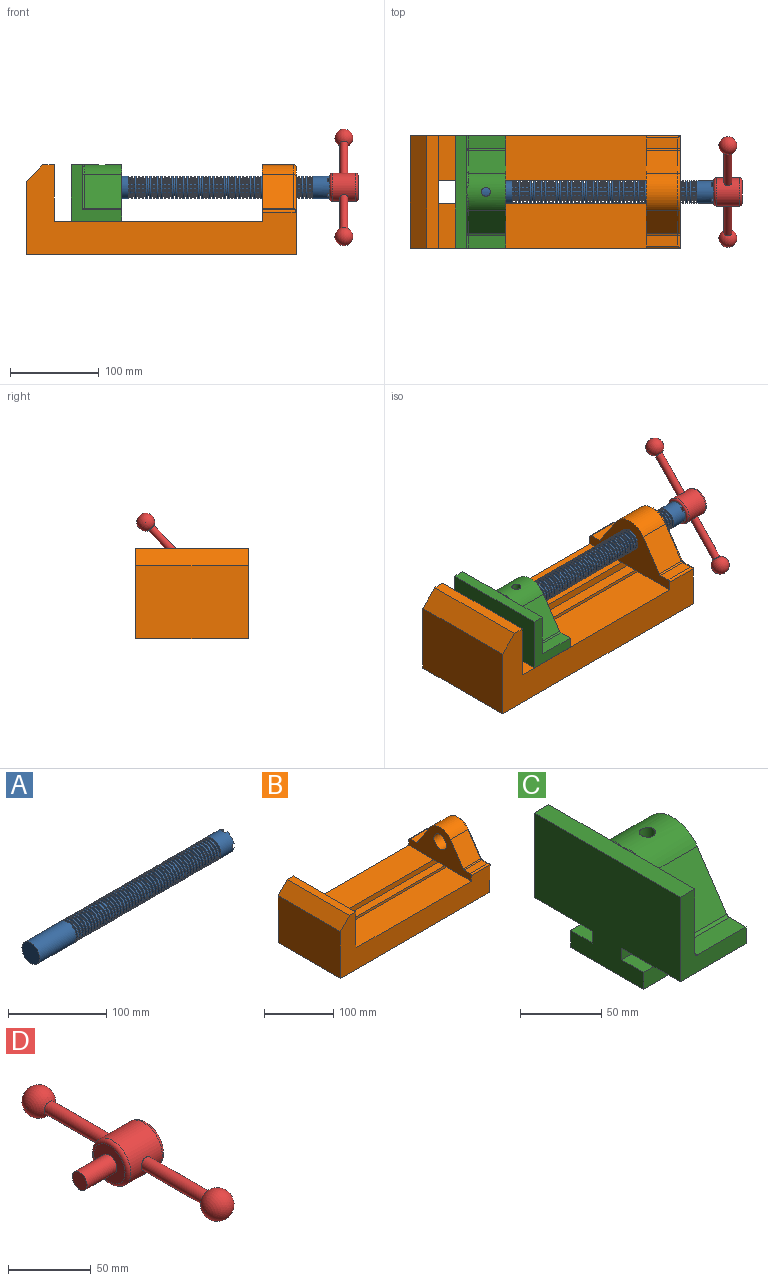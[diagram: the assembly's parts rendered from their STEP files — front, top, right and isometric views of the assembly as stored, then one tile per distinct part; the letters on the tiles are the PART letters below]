
ASSEMBLY  parts=4 mates=4
PART A: 220 faces, bbox 279.4x25.4x25.4 mm
  f0: cylinder r=12.7mm len=25.4mm, axis (-1,0,0), area 1468.2mm2, adj f1,f2,f3,f5,f7,f208,f209,f210
  f1: plane 9.9x9.9mm, normal (1,0,0), area 62.3mm2, adj f0,f4,f213,f216
  f2: plane 9.9x9.9mm, normal (1,0,0), area 62.3mm2, adj f0,f4,f210,f218
  f3: plane 9.9x9.9mm, normal (1,0,0), area 62.3mm2, adj f0,f4,f209,f212
  f4: cylinder r=6.35mm len=25.4mm, axis (1,0,0), area 960.3mm2, adj f1,f2,f3,f5,f6,f208,f209,f210
  f5: plane 9.9x9.9mm, normal (1,0,0), area 62.3mm2, adj f0,f4,f215,f217
  f6: plane 12.7x12.7mm, normal (1,0,0), area 126.7mm2, adj f4
  f7: cone r=12.7mm half-angle=76deg, axis (1,0,0), area 188mm2, adj f0,f9
  f8: cone r=10.16mm half-angle=76deg, axis (-1,0,0), area 188mm2, adj f9,f10
  f9: cylinder r=10.16mm len=20.32mm, axis (1,0,0), area 81.1mm2, adj f7,f8
  f10: cylinder r=12.7mm len=25.4mm, axis (-1,0,0), area 131.7mm2, adj f8,f11
  f11: cone r=12.7mm half-angle=76deg, axis (1,0,0), area 188mm2, adj f10,f13
  f12: cone r=10.16mm half-angle=76deg, axis (-1,0,0), area 188mm2, adj f13,f14
  f13: cylinder r=10.16mm len=20.32mm, axis (1,0,0), area 81.1mm2, adj f11,f12
  f14: cylinder r=12.7mm len=25.4mm, axis (-1,0,0), area 131.7mm2, adj f12,f15
  f15: cone r=12.7mm half-angle=76deg, axis (1,0,0), area 188mm2, adj f14,f17
  f16: cone r=10.16mm half-angle=76deg, axis (-1,0,0), area 188mm2, adj f17,f18
  f17: cylinder r=10.16mm len=20.32mm, axis (1,0,0), area 81.1mm2, adj f15,f16
  f18: cylinder r=12.7mm len=25.4mm, axis (-1,0,0), area 131.7mm2, adj f16,f19
  f19: cone r=12.7mm half-angle=76deg, axis (1,0,0), area 188mm2, adj f18,f21
  f20: cone r=10.16mm half-angle=76deg, axis (-1,0,0), area 188mm2, adj f21,f22
  f21: cylinder r=10.16mm len=20.32mm, axis (1,0,0), area 81.1mm2, adj f19,f20
  f22: cylinder r=12.7mm len=25.4mm, axis (-1,0,0), area 131.7mm2, adj f20,f23
  f23: cone r=12.7mm half-angle=76deg, axis (1,0,0), area 188mm2, adj f22,f25
  f24: cone r=10.16mm half-angle=76deg, axis (-1,0,0), area 188mm2, adj f25,f26
  f25: cylinder r=10.16mm len=20.32mm, axis (1,0,0), area 81.1mm2, adj f23,f24
  f26: cylinder r=12.7mm len=25.4mm, axis (-1,0,0), area 131.7mm2, adj f24,f27
  f27: cone r=12.7mm half-angle=76deg, axis (1,0,0), area 188mm2, adj f26,f29
  f28: cone r=10.16mm half-angle=76deg, axis (-1,0,0), area 188mm2, adj f29,f30
  f29: cylinder r=10.16mm len=20.32mm, axis (1,0,0), area 81.1mm2, adj f27,f28
  f30: cylinder r=12.7mm len=25.4mm, axis (-1,0,0), area 131.7mm2, adj f28,f31
  f31: cone r=12.7mm half-angle=76deg, axis (1,0,0), area 188mm2, adj f30,f33
  f32: cone r=10.16mm half-angle=76deg, axis (-1,0,0), area 188mm2, adj f33,f34
  f33: cylinder r=10.16mm len=20.32mm, axis (1,0,0), area 81.1mm2, adj f31,f32
  f34: cylinder r=12.7mm len=25.4mm, axis (-1,0,0), area 131.7mm2, adj f32,f35
  f35: cone r=12.7mm half-angle=76deg, axis (1,0,0), area 188mm2, adj f34,f37
  f36: cone r=10.16mm half-angle=76deg, axis (-1,0,0), area 188mm2, adj f37,f38
  f37: cylinder r=10.16mm len=20.32mm, axis (1,0,0), area 81.1mm2, adj f35,f36
  f38: cylinder r=12.7mm len=25.4mm, axis (-1,0,0), area 131.7mm2, adj f36,f39
  f39: cone r=12.7mm half-angle=76deg, axis (1,0,0), area 188mm2, adj f38,f41
  f40: cone r=10.16mm half-angle=76deg, axis (-1,0,0), area 188mm2, adj f41,f42
  f41: cylinder r=10.16mm len=20.32mm, axis (1,0,0), area 81.1mm2, adj f39,f40
  f42: cylinder r=12.7mm len=25.4mm, axis (-1,0,0), area 131.7mm2, adj f40,f43
  f43: cone r=12.7mm half-angle=76deg, axis (1,0,0), area 188mm2, adj f42,f45
  f44: cone r=10.16mm half-angle=76deg, axis (-1,0,0), area 188mm2, adj f45,f46
  f45: cylinder r=10.16mm len=20.32mm, axis (1,0,0), area 81.1mm2, adj f43,f44
  f46: cylinder r=12.7mm len=25.4mm, axis (-1,0,0), area 131.7mm2, adj f44,f47
  f47: cone r=12.7mm half-angle=76deg, axis (1,0,0), area 188mm2, adj f46,f49
  f48: cone r=10.16mm half-angle=76deg, axis (-1,0,0), area 188mm2, adj f49,f50
  f49: cylinder r=10.16mm len=20.32mm, axis (1,0,0), area 81.1mm2, adj f47,f48
  f50: cylinder r=12.7mm len=25.4mm, axis (-1,0,0), area 131.7mm2, adj f48,f51
  f51: cone r=12.7mm half-angle=76deg, axis (1,0,0), area 188mm2, adj f50,f53
  f52: cone r=10.16mm half-angle=76deg, axis (-1,0,0), area 188mm2, adj f53,f54
  f53: cylinder r=10.16mm len=20.32mm, axis (1,0,0), area 81.1mm2, adj f51,f52
  f54: cylinder r=12.7mm len=25.4mm, axis (-1,0,0), area 131.7mm2, adj f52,f55
  f55: cone r=12.7mm half-angle=76deg, axis (1,0,0), area 188mm2, adj f54,f57
  f56: cone r=10.16mm half-angle=76deg, axis (-1,0,0), area 188mm2, adj f57,f58
  f57: cylinder r=10.16mm len=20.32mm, axis (1,0,0), area 81.1mm2, adj f55,f56
  f58: cylinder r=12.7mm len=25.4mm, axis (-1,0,0), area 131.7mm2, adj f56,f59
  f59: cone r=12.7mm half-angle=76deg, axis (1,0,0), area 188mm2, adj f58,f61
  f60: cone r=10.16mm half-angle=76deg, axis (-1,0,0), area 188mm2, adj f61,f62
  f61: cylinder r=10.16mm len=20.32mm, axis (1,0,0), area 81.1mm2, adj f59,f60
  f62: cylinder r=12.7mm len=25.4mm, axis (-1,0,0), area 131.7mm2, adj f60,f63
  f63: cone r=12.7mm half-angle=76deg, axis (1,0,0), area 188mm2, adj f62,f65
  f64: cone r=10.16mm half-angle=76deg, axis (-1,0,0), area 188mm2, adj f65,f66
  f65: cylinder r=10.16mm len=20.32mm, axis (1,0,0), area 81.1mm2, adj f63,f64
  f66: cylinder r=12.7mm len=25.4mm, axis (-1,0,0), area 131.7mm2, adj f64,f67
  f67: cone r=12.7mm half-angle=76deg, axis (1,0,0), area 188mm2, adj f66,f69
  f68: cone r=10.16mm half-angle=76deg, axis (-1,0,0), area 188mm2, adj f69,f70
  f69: cylinder r=10.16mm len=20.32mm, axis (1,0,0), area 81.1mm2, adj f67,f68
  f70: cylinder r=12.7mm len=25.4mm, axis (-1,0,0), area 131.7mm2, adj f68,f71
  f71: cone r=12.7mm half-angle=76deg, axis (1,0,0), area 188mm2, adj f70,f73
  f72: cone r=10.16mm half-angle=76deg, axis (-1,0,0), area 188mm2, adj f73,f74
  f73: cylinder r=10.16mm len=20.32mm, axis (1,0,0), area 81.1mm2, adj f71,f72
  f74: cylinder r=12.7mm len=25.4mm, axis (-1,0,0), area 131.7mm2, adj f72,f75
  f75: cone r=12.7mm half-angle=76deg, axis (1,0,0), area 188mm2, adj f74,f77
  f76: cone r=10.16mm half-angle=76deg, axis (-1,0,0), area 188mm2, adj f77,f78
  f77: cylinder r=10.16mm len=20.32mm, axis (1,0,0), area 81.1mm2, adj f75,f76
  f78: cylinder r=12.7mm len=25.4mm, axis (-1,0,0), area 131.7mm2, adj f76,f79
  f79: cone r=12.7mm half-angle=76deg, axis (1,0,0), area 188mm2, adj f78,f81
  f80: cone r=10.16mm half-angle=76deg, axis (-1,0,0), area 188mm2, adj f81,f82
  f81: cylinder r=10.16mm len=20.32mm, axis (1,0,0), area 81.1mm2, adj f79,f80
  f82: cylinder r=12.7mm len=25.4mm, axis (-1,0,0), area 131.7mm2, adj f80,f83
  f83: cone r=12.7mm half-angle=76deg, axis (1,0,0), area 188mm2, adj f82,f85
  f84: cone r=10.16mm half-angle=76deg, axis (-1,0,0), area 188mm2, adj f85,f86
  f85: cylinder r=10.16mm len=20.32mm, axis (1,0,0), area 81.1mm2, adj f83,f84
  f86: cylinder r=12.7mm len=25.4mm, axis (-1,0,0), area 131.7mm2, adj f84,f87
  f87: cone r=12.7mm half-angle=76deg, axis (1,0,0), area 188mm2, adj f86,f89
  f88: cone r=10.16mm half-angle=76deg, axis (-1,0,0), area 188mm2, adj f89,f90
  f89: cylinder r=10.16mm len=20.32mm, axis (1,0,0), area 81.1mm2, adj f87,f88
  f90: cylinder r=12.7mm len=25.4mm, axis (-1,0,0), area 131.7mm2, adj f88,f91
  f91: cone r=12.7mm half-angle=76deg, axis (1,0,0), area 188mm2, adj f90,f93
  f92: cone r=10.16mm half-angle=76deg, axis (-1,0,0), area 188mm2, adj f93,f94
  f93: cylinder r=10.16mm len=20.32mm, axis (1,0,0), area 81.1mm2, adj f91,f92
  f94: cylinder r=12.7mm len=25.4mm, axis (-1,0,0), area 131.7mm2, adj f92,f95
  f95: cone r=12.7mm half-angle=76deg, axis (1,0,0), area 188mm2, adj f94,f97
  f96: cone r=10.16mm half-angle=76deg, axis (-1,0,0), area 188mm2, adj f97,f98
  f97: cylinder r=10.16mm len=20.32mm, axis (1,0,0), area 81.1mm2, adj f95,f96
  f98: cylinder r=12.7mm len=25.4mm, axis (-1,0,0), area 131.7mm2, adj f96,f99
  f99: cone r=12.7mm half-angle=76deg, axis (1,0,0), area 188mm2, adj f98,f101
  f100: cone r=10.16mm half-angle=76deg, axis (-1,0,0), area 188mm2, adj f101,f102
  f101: cylinder r=10.16mm len=20.32mm, axis (1,0,0), area 81.1mm2, adj f99,f100
  f102: cylinder r=12.7mm len=25.4mm, axis (-1,0,0), area 131.7mm2, adj f100,f103
  f103: cone r=12.7mm half-angle=76deg, axis (1,0,0), area 188mm2, adj f102,f105
  f104: cone r=10.16mm half-angle=76deg, axis (-1,0,0), area 188mm2, adj f105,f106
  f105: cylinder r=10.16mm len=20.32mm, axis (1,0,0), area 81.1mm2, adj f103,f104
  f106: cylinder r=12.7mm len=25.4mm, axis (-1,0,0), area 131.7mm2, adj f104,f107
  f107: cone r=12.7mm half-angle=76deg, axis (1,0,0), area 188mm2, adj f106,f109
  f108: cone r=10.16mm half-angle=76deg, axis (-1,0,0), area 188mm2, adj f109,f110
  f109: cylinder r=10.16mm len=20.32mm, axis (1,0,0), area 81.1mm2, adj f107,f108
  f110: cylinder r=12.7mm len=25.4mm, axis (-1,0,0), area 131.7mm2, adj f108,f111
  f111: cone r=12.7mm half-angle=76deg, axis (1,0,0), area 188mm2, adj f110,f113
  f112: cone r=10.16mm half-angle=76deg, axis (-1,0,0), area 188mm2, adj f113,f114
  f113: cylinder r=10.16mm len=20.32mm, axis (1,0,0), area 81.1mm2, adj f111,f112
  f114: cylinder r=12.7mm len=25.4mm, axis (-1,0,0), area 131.7mm2, adj f112,f115
  f115: cone r=12.7mm half-angle=76deg, axis (1,0,0), area 188mm2, adj f114,f117
  f116: cone r=10.16mm half-angle=76deg, axis (-1,0,0), area 188mm2, adj f117,f118
  f117: cylinder r=10.16mm len=20.32mm, axis (1,0,0), area 81.1mm2, adj f115,f116
  f118: cylinder r=12.7mm len=25.4mm, axis (-1,0,0), area 131.7mm2, adj f116,f119
  f119: cone r=12.7mm half-angle=76deg, axis (1,0,0), area 188mm2, adj f118,f121
  f120: cone r=10.16mm half-angle=76deg, axis (-1,0,0), area 188mm2, adj f121,f122
  f121: cylinder r=10.16mm len=20.32mm, axis (1,0,0), area 81.1mm2, adj f119,f120
  f122: cylinder r=12.7mm len=25.4mm, axis (-1,0,0), area 131.7mm2, adj f120,f123
  f123: cone r=12.7mm half-angle=76deg, axis (1,0,0), area 188mm2, adj f122,f125
  f124: cone r=10.16mm half-angle=76deg, axis (-1,0,0), area 188mm2, adj f125,f126
  f125: cylinder r=10.16mm len=20.32mm, axis (1,0,0), area 81.1mm2, adj f123,f124
  f126: cylinder r=12.7mm len=25.4mm, axis (-1,0,0), area 131.7mm2, adj f124,f127
  f127: cone r=12.7mm half-angle=76deg, axis (1,0,0), area 188mm2, adj f126,f129
  f128: cone r=10.16mm half-angle=76deg, axis (-1,0,0), area 188mm2, adj f129,f130
  f129: cylinder r=10.16mm len=20.32mm, axis (1,0,0), area 81.1mm2, adj f127,f128
  f130: cylinder r=12.7mm len=25.4mm, axis (-1,0,0), area 131.7mm2, adj f128,f131
  f131: cone r=12.7mm half-angle=76deg, axis (1,0,0), area 188mm2, adj f130,f133
  f132: cone r=10.16mm half-angle=76deg, axis (-1,0,0), area 188mm2, adj f133,f134
  f133: cylinder r=10.16mm len=20.32mm, axis (1,0,0), area 81.1mm2, adj f131,f132
  f134: cylinder r=12.7mm len=25.4mm, axis (-1,0,0), area 131.7mm2, adj f132,f135
  f135: cone r=12.7mm half-angle=76deg, axis (1,0,0), area 188mm2, adj f134,f137
  f136: cone r=10.16mm half-angle=76deg, axis (-1,0,0), area 188mm2, adj f137,f138
  f137: cylinder r=10.16mm len=20.32mm, axis (1,0,0), area 81.1mm2, adj f135,f136
  f138: cylinder r=12.7mm len=25.4mm, axis (-1,0,0), area 131.7mm2, adj f136,f139
  f139: cone r=12.7mm half-angle=76deg, axis (1,0,0), area 188mm2, adj f138,f141
  f140: cone r=10.16mm half-angle=76deg, axis (-1,0,0), area 188mm2, adj f141,f142
  f141: cylinder r=10.16mm len=20.32mm, axis (1,0,0), area 81.1mm2, adj f139,f140
  f142: cylinder r=12.7mm len=25.4mm, axis (-1,0,0), area 131.7mm2, adj f140,f143
  f143: cone r=12.7mm half-angle=76deg, axis (1,0,0), area 188mm2, adj f142,f145
  f144: cone r=10.16mm half-angle=76deg, axis (-1,0,0), area 188mm2, adj f145,f146
  f145: cylinder r=10.16mm len=20.32mm, axis (1,0,0), area 81.1mm2, adj f143,f144
  f146: cylinder r=12.7mm len=25.4mm, axis (-1,0,0), area 131.7mm2, adj f144,f147
  f147: cone r=12.7mm half-angle=76deg, axis (1,0,0), area 188mm2, adj f146,f149
  f148: cone r=10.16mm half-angle=76deg, axis (-1,0,0), area 188mm2, adj f149,f150
  f149: cylinder r=10.16mm len=20.32mm, axis (1,0,0), area 81.1mm2, adj f147,f148
  f150: cylinder r=12.7mm len=25.4mm, axis (-1,0,0), area 131.7mm2, adj f148,f151
  f151: cone r=12.7mm half-angle=76deg, axis (1,0,0), area 188mm2, adj f150,f153
  f152: cone r=10.16mm half-angle=76deg, axis (-1,0,0), area 188mm2, adj f153,f154
  f153: cylinder r=10.16mm len=20.32mm, axis (1,0,0), area 81.1mm2, adj f151,f152
  f154: cylinder r=12.7mm len=25.4mm, axis (-1,0,0), area 131.7mm2, adj f152,f155
  f155: cone r=12.7mm half-angle=76deg, axis (1,0,0), area 188mm2, adj f154,f157
  f156: cone r=10.16mm half-angle=76deg, axis (-1,0,0), area 188mm2, adj f157,f158
  f157: cylinder r=10.16mm len=20.32mm, axis (1,0,0), area 81.1mm2, adj f155,f156
  f158: cylinder r=12.7mm len=25.4mm, axis (-1,0,0), area 131.7mm2, adj f156,f159
  f159: cone r=12.7mm half-angle=76deg, axis (1,0,0), area 188mm2, adj f158,f161
  f160: cone r=10.16mm half-angle=76deg, axis (-1,0,0), area 188mm2, adj f161,f162
  f161: cylinder r=10.16mm len=20.32mm, axis (1,0,0), area 81.1mm2, adj f159,f160
  f162: cylinder r=12.7mm len=25.4mm, axis (-1,0,0), area 131.7mm2, adj f160,f163
  f163: cone r=12.7mm half-angle=76deg, axis (1,0,0), area 188mm2, adj f162,f165
  f164: cone r=10.16mm half-angle=76deg, axis (-1,0,0), area 188mm2, adj f165,f166
  f165: cylinder r=10.16mm len=20.32mm, axis (1,0,0), area 81.1mm2, adj f163,f164
  f166: cylinder r=12.7mm len=25.4mm, axis (-1,0,0), area 131.7mm2, adj f164,f167
  f167: cone r=12.7mm half-angle=76deg, axis (1,0,0), area 188mm2, adj f166,f169
  f168: cone r=10.16mm half-angle=76deg, axis (-1,0,0), area 188mm2, adj f169,f170
  f169: cylinder r=10.16mm len=20.32mm, axis (1,0,0), area 81.1mm2, adj f167,f168
  f170: cylinder r=12.7mm len=25.4mm, axis (-1,0,0), area 131.7mm2, adj f168,f171
  f171: cone r=12.7mm half-angle=76deg, axis (1,0,0), area 188mm2, adj f170,f173
  f172: cone r=10.16mm half-angle=76deg, axis (-1,0,0), area 188mm2, adj f173,f174
  f173: cylinder r=10.16mm len=20.32mm, axis (1,0,0), area 81.1mm2, adj f171,f172
  f174: cylinder r=12.7mm len=25.4mm, axis (-1,0,0), area 131.7mm2, adj f172,f175
  f175: cone r=12.7mm half-angle=76deg, axis (1,0,0), area 188mm2, adj f174,f177
  f176: cone r=10.16mm half-angle=76deg, axis (-1,0,0), area 188mm2, adj f177,f178
  f177: cylinder r=10.16mm len=20.32mm, axis (1,0,0), area 81.1mm2, adj f175,f176
  f178: cylinder r=12.7mm len=25.4mm, axis (-1,0,0), area 131.7mm2, adj f176,f179
  f179: cone r=12.7mm half-angle=76deg, axis (1,0,0), area 188mm2, adj f178,f181
  f180: cone r=10.16mm half-angle=76deg, axis (-1,0,0), area 188mm2, adj f181,f182
  f181: cylinder r=10.16mm len=20.32mm, axis (1,0,0), area 81.1mm2, adj f179,f180
  f182: cylinder r=12.7mm len=25.4mm, axis (-1,0,0), area 131.7mm2, adj f180,f183
  f183: cone r=12.7mm half-angle=76deg, axis (1,0,0), area 188mm2, adj f182,f185
  f184: cone r=10.16mm half-angle=76deg, axis (-1,0,0), area 188mm2, adj f185,f186
  f185: cylinder r=10.16mm len=20.32mm, axis (1,0,0), area 81.1mm2, adj f183,f184
  f186: cylinder r=12.7mm len=25.4mm, axis (-1,0,0), area 131.7mm2, adj f184,f187
  f187: cone r=12.7mm half-angle=76deg, axis (1,0,0), area 188mm2, adj f186,f189
  f188: cone r=10.16mm half-angle=76deg, axis (-1,0,0), area 188mm2, adj f189,f190
  f189: cylinder r=10.16mm len=20.32mm, axis (1,0,0), area 81.1mm2, adj f187,f188
  f190: cylinder r=12.7mm len=25.4mm, axis (-1,0,0), area 131.7mm2, adj f188,f191
  f191: cone r=12.7mm half-angle=76deg, axis (1,0,0), area 188mm2, adj f190,f193
  f192: cone r=10.16mm half-angle=76deg, axis (-1,0,0), area 188mm2, adj f193,f194
  f193: cylinder r=10.16mm len=20.32mm, axis (1,0,0), area 81.1mm2, adj f191,f192
  f194: cylinder r=12.7mm len=25.4mm, axis (-1,0,0), area 131.7mm2, adj f192,f195
  f195: cone r=12.7mm half-angle=76deg, axis (1,0,0), area 188mm2, adj f194,f197
  f196: cone r=10.16mm half-angle=76deg, axis (-1,0,0), area 188mm2, adj f197,f198
  f197: cylinder r=10.16mm len=20.32mm, axis (1,0,0), area 81.1mm2, adj f195,f196
  f198: cylinder r=12.7mm len=25.4mm, axis (-1,0,0), area 131.7mm2, adj f196,f199
  f199: cone r=12.7mm half-angle=76deg, axis (1,0,0), area 188mm2, adj f198,f201
  f200: cone r=10.16mm half-angle=76deg, axis (-1,0,0), area 188mm2, adj f201,f202
  f201: cylinder r=10.16mm len=20.32mm, axis (1,0,0), area 81.1mm2, adj f199,f200
  f202: cylinder r=12.7mm len=25.4mm, axis (-1,0,0), area 131.7mm2, adj f200,f203
  f203: cone r=12.7mm half-angle=76deg, axis (1,0,0), area 188mm2, adj f202,f205
  f204: cone r=10.16mm half-angle=76deg, axis (-1,0,0), area 188mm2, adj f205,f207
  f205: cylinder r=10.16mm len=20.32mm, axis (1,0,0), area 81.1mm2, adj f203,f204
  f206: plane 25.4x25.4mm, normal (-1,0,0), area 506.7mm2, adj f207
  f207: cylinder r=12.7mm len=52.45mm, axis (-1,0,0), area 4185.4mm2, adj f204,f206
  f208: plane 6.88x5.08mm, normal (1,0,0), area 32.7mm2, adj f0,f4,f209,f210
  f209: plane 6.62x2.54mm, normal (0,-1,0), area 16.8mm2, adj f0,f3,f4,f208
  f210: plane 6.62x2.54mm, normal (0,1,0), area 16.8mm2, adj f0,f2,f4,f208
  f211: plane 6.88x5.08mm, normal (1,0,0), area 32.7mm2, adj f0,f4,f212,f213
  f212: plane 6.62x2.54mm, normal (0,0,1), area 16.8mm2, adj f0,f3,f4,f211
  f213: plane 6.62x2.54mm, normal (0,0,-1), area 16.8mm2, adj f0,f1,f4,f211
  f214: plane 6.88x5.08mm, normal (1,0,0), area 32.7mm2, adj f0,f4,f215,f216
  f215: plane 6.62x2.54mm, normal (0,1,0), area 16.8mm2, adj f0,f4,f5,f214
  f216: plane 6.62x2.54mm, normal (0,-1,0), area 16.8mm2, adj f0,f1,f4,f214
  f217: plane 6.62x2.54mm, normal (0,0,-1), area 16.8mm2, adj f0,f4,f5,f219
  f218: plane 6.62x2.54mm, normal (0,0,1), area 16.8mm2, adj f0,f2,f4,f219
  f219: plane 6.88x5.08mm, normal (1,0,0), area 32.7mm2, adj f0,f4,f217,f218
PART B: 39 faces, bbox 304.8x127x103.7 mm
  f0: plane 234.95x50.8mm, normal (0,0,1), area 11935.5mm2, adj f2,f8,f16,f26
  f1: plane 234.95x50.8mm, normal (0,0,1), area 11935.5mm2, adj f2,f9,f16,f27
  f2: plane 127x101.6mm, normal (1,0,0), area 9516.1mm2, adj f0,f1,f3,f6,f8,f9,f18,f19
  f3: plane 127x12.7mm, normal (0,0,1), area 1612.9mm2, adj f2,f4,f8,f9
  f4: plane 127x19.05mm, normal (-0.71,0,0.71), area 3421.5mm2, adj f3,f5,f8,f9
  f5: plane 127x82.55mm, normal (-1,0,0), area 10483.9mm2, adj f4,f6,f8,f9
  f6: plane 304.8x127mm, normal (0,0,-1), area 31774.1mm2, adj f2,f5,f7,f8,f9,f21,f22
  f7: plane 127x99.06mm, normal (1,0,0), area 7097.5mm2, adj f6,f8,f9,f14,f17,f18,f19,f20
  f8: plane 304.8x101.6mm, normal (0,-1,0), area 13834.6mm2, adj f0,f2,f3,f4,f5,f6,f7,f16
  f9: plane 304.8x101.6mm, normal (0,1,0), area 13834.6mm2, adj f1,f2,f3,f4,f5,f6,f7,f16
  f10: plane 35.56x11.98mm, normal (0,0,1), area 426mm2, adj f16,f28,f29,f30
  f11: plane 38.43x35.56mm, normal (0,0.83,0.56), area 1645.4mm2, adj f12,f16,f29,f32
  f12: cylinder r=25.4mm len=42.19mm, axis (1,0,0), area 1770.2mm2, adj f11,f13,f16,f33
  f13: plane 38.43x35.56mm, normal (0,-0.83,0.56), area 1645.4mm2, adj f12,f16,f34,f35
  f14: cylinder r=12.7mm len=38.1mm, axis (1,0,0), area 3040.2mm2, adj f7,f16
  f15: plane 35.56x11.98mm, normal (0,0,1), area 426mm2, adj f16,f34,f36,f38
  f16: plane 127x63.5mm, normal (-1,0,0), area 4155.5mm2, adj f0,f1,f8,f9,f10,f11,f12,f13
  f17: plane 38.1x25.4mm, normal (0,0,-1), area 967.7mm2, adj f7,f16,f26,f27
  f18: plane 273.05x19.05mm, normal (0,0,-1), area 5201.6mm2, adj f2,f7,f19,f26
  f19: plane 273.05x12.7mm, normal (0,1,0), area 3467.7mm2, adj f2,f7,f18,f20
  f20: plane 273.05x19.05mm, normal (0,0,1), area 5201.6mm2, adj f2,f7,f19,f21
  f21: plane 273.05x16.51mm, normal (0,1,0), area 4508.1mm2, adj f2,f6,f7,f20
  f22: plane 273.05x16.51mm, normal (0,-1,0), area 4508.1mm2, adj f2,f6,f7,f23
  f23: plane 273.05x19.05mm, normal (0,0,1), area 5201.6mm2, adj f2,f7,f22,f24
  f24: plane 273.05x12.7mm, normal (0,-1,0), area 3467.7mm2, adj f2,f7,f23,f25
  f25: plane 273.05x19.05mm, normal (0,0,-1), area 5201.6mm2, adj f2,f7,f24,f27
  f26: plane 273.05x8.89mm, normal (0,1,0), area 2427.4mm2, adj f0,f2,f7,f17,f18
  f27: plane 273.05x8.89mm, normal (0,-1,0), area 2427.4mm2, adj f1,f2,f7,f17,f25
  f28: cylinder r=2.54mm len=38.1mm, axis (1,0,0), area 148.3mm2, adj f9,f10,f16,f30
  f29: cylinder r=2.54mm len=35.56mm, axis (-1,0,0), area 88.5mm2, adj f10,f11,f16,f31
  f30: cylinder r=2.54mm len=14.52mm, axis (0,1,0), area 54.3mm2, adj f7,f10,f28,f31
  f31: torus R=5.08mm, axis (-1,0,0), area 13.5mm2, adj f7,f29,f30,f32
  f32: cylinder r=2.54mm len=39.84mm, axis (0,0.56,-0.83), area 184.6mm2, adj f7,f11,f31,f33
  f33: torus R=22.86mm, axis (-1,0,0), area 191.4mm2, adj f7,f12,f32,f35
  f34: cylinder r=2.54mm len=35.56mm, axis (-1,0,0), area 88.5mm2, adj f13,f15,f16,f37
  f35: cylinder r=2.54mm len=39.84mm, axis (0,0.56,0.83), area 184.6mm2, adj f7,f13,f33,f37
  f36: cylinder r=2.54mm len=38.1mm, axis (-1,0,0), area 148.3mm2, adj f8,f15,f16,f38
  f37: torus R=5.08mm, axis (-1,0,0), area 13.5mm2, adj f7,f34,f35,f38
  f38: cylinder r=2.54mm len=14.52mm, axis (0,1,0), area 54.3mm2, adj f7,f15,f36,f37
PART C: 36 faces, bbox 57.2x127x89 mm
  f0: plane 57.15x50.8mm, normal (0,0,-1), area 2903.2mm2, adj f6,f9,f10,f23
  f1: cylinder r=12.7mm len=44.45mm, axis (1,0,0), area 3464.3mm2, adj f6,f15,f16
  f2: plane 41.91x14.52mm, normal (0,0,1), area 608.5mm2, adj f6,f11,f24,f25
  f3: plane 51.86x48.26mm, normal (1,0,0), area 1495.7mm2, adj f8,f10,f31,f33,f35
  f4: plane 51.86x48.26mm, normal (1,0,0), area 1495.7mm2, adj f8,f11,f24,f28,f29
  f5: plane 57.15x50.8mm, normal (0,0,-1), area 2903.2mm2, adj f6,f9,f11,f22
  f6: plane 127x85.09mm, normal (1,0,0), area 5190.6mm2, adj f0,f1,f2,f5,f7,f10,f11,f12
  f7: plane 41.91x14.52mm, normal (0,0,1), area 608.5mm2, adj f6,f10,f30,f31
  f8: plane 127x12.7mm, normal (0,0,1), area 1612.9mm2, adj f3,f4,f9,f10,f11,f26,f34
  f9: plane 127x85.09mm, normal (-1,0,0), area 9096.8mm2, adj f0,f5,f8,f10,f11,f17,f18,f19
  f10: plane 63.5x57.15mm, normal (0,-1,0), area 1372.3mm2, adj f0,f3,f6,f7,f8,f9,f31
  f11: plane 63.5x57.15mm, normal (0,1,0), area 1372.3mm2, adj f2,f4,f5,f6,f8,f9,f24
  f12: plane 41.91x38.43mm, normal (0,-0.83,0.56), area 1939.2mm2, adj f6,f13,f30,f33
  f13: cylinder r=25.4mm len=44.45mm, axis (1,0,0), area 2026.5mm2, adj f6,f12,f14,f16,f26,f28,f34,f35
  f14: plane 41.91x38.43mm, normal (0,0.83,0.56), area 1939.2mm2, adj f6,f13,f25,f29
  f15: plane 25.4x25.4mm, normal (1,0,0), area 506.7mm2, adj f1
  f16: cylinder r=5.08mm len=13.76mm, axis (0,0,1), area 414mm2, adj f1,f13
  f17: plane 57.15x19.05mm, normal (0,0,1), area 1088.7mm2, adj f6,f9,f18,f23
  f18: plane 57.15x12.7mm, normal (0,-1,0), area 725.8mm2, adj f6,f9,f17,f19
  f19: plane 63.5x57.15mm, normal (0,0,-1), area 3629mm2, adj f6,f9,f18,f20
  f20: plane 57.15x12.7mm, normal (0,1,0), area 725.8mm2, adj f6,f9,f19,f21
  f21: plane 57.15x19.05mm, normal (0,0,1), area 1088.7mm2, adj f6,f9,f20,f22
  f22: plane 57.15x8.89mm, normal (0,1,0), area 508.1mm2, adj f5,f6,f9,f21
  f23: plane 57.15x8.89mm, normal (0,-1,0), area 508.1mm2, adj f0,f6,f9,f17
  f24: cylinder r=2.54mm len=14.52mm, axis (0,-1,0), area 57.9mm2, adj f2,f4,f11,f27
  f25: cylinder r=2.54mm len=41.91mm, axis (1,0,0), area 104.3mm2, adj f2,f6,f14,f27
  f26: bspline ~12.24x2.8mm, area 20.9mm2, adj f8,f13,f28
  f27: sphere r=2.54mm, area 6.3mm2, adj f24,f25,f29
  f28: torus R=27.94mm, axis (1,0,0), area 57.8mm2, adj f4,f13,f26,f29
  f29: cylinder r=2.54mm len=39.84mm, axis (0,-0.56,0.83), area 184.6mm2, adj f4,f14,f27,f28
  f30: cylinder r=2.54mm len=41.91mm, axis (1,0,0), area 104.3mm2, adj f6,f7,f12,f32
  f31: cylinder r=2.54mm len=14.52mm, axis (0,-1,0), area 57.9mm2, adj f3,f7,f10,f32
  f32: sphere r=2.54mm, area 6.3mm2, adj f30,f31,f33
  f33: cylinder r=2.54mm len=39.84mm, axis (0,-0.56,-0.83), area 184.6mm2, adj f3,f12,f32,f35
  f34: bspline ~12.24x2.8mm, area 20.9mm2, adj f8,f13,f35
  f35: torus R=27.94mm, axis (1,0,0), area 57.8mm2, adj f3,f13,f33,f34
PART D: 11 faces, bbox 57.2x172.7x34.4 mm
  f0: sphere r=10.16mm, area 1231.8mm2, adj f1
  f1: cylinder r=4.45mm len=51.82mm, axis (0,1,0), area 1438.5mm2, adj f0,f4
  f2: sphere r=10.16mm, area 1231.8mm2, adj f3
  f3: cylinder r=4.45mm len=51.82mm, axis (0,1,0), area 1438.5mm2, adj f2,f4
  f4: cylinder r=15.88mm len=31.75mm, axis (-1,0,0), area 2534.7mm2, adj f1,f3,f9,f10
  f5: cylinder r=6.35mm len=25.4mm, axis (-1,0,0), area 1013.4mm2, adj f6,f8
  f6: plane 12.7x12.7mm, normal (-1,0,0), area 126.7mm2, adj f5
  f7: plane 26.67x26.67mm, normal (1,0,0), area 558.6mm2, adj f10
  f8: plane 26.67x26.67mm, normal (-1,0,0), area 432mm2, adj f5,f9
  f9: torus R=13.33mm, axis (1,0,0), area 374.8mm2, adj f4,f8
  f10: torus R=13.33mm, axis (1,0,0), area 374.8mm2, adj f4,f7
PLACE A rot(axis=(1,0,0),46.8deg) t=(19.05,55.55,24.04)mm
PLACE B at identity fixed
PLACE C t=(19.05,0,0)mm
PLACE D rot(axis=(1,0,0),46.8deg) t=(19.05,55.55,24.04)mm
MATE cylindrical A.f7 <-> B.f12  axis (-1,0,0) through (-188.85,0,76.2)mm
MATE revolute C.f28 <-> A.f7  axis (1,0,0) through (-241.3,0,76.2)mm
MATE slider B.f2 <-> C.f9  axis (-1,0,0) through (-273.05,-63.5,38.1)mm
MATE fastened A.f4 <-> D.f4  axis (1,0,0) through (38.1,0,76.2)mm
